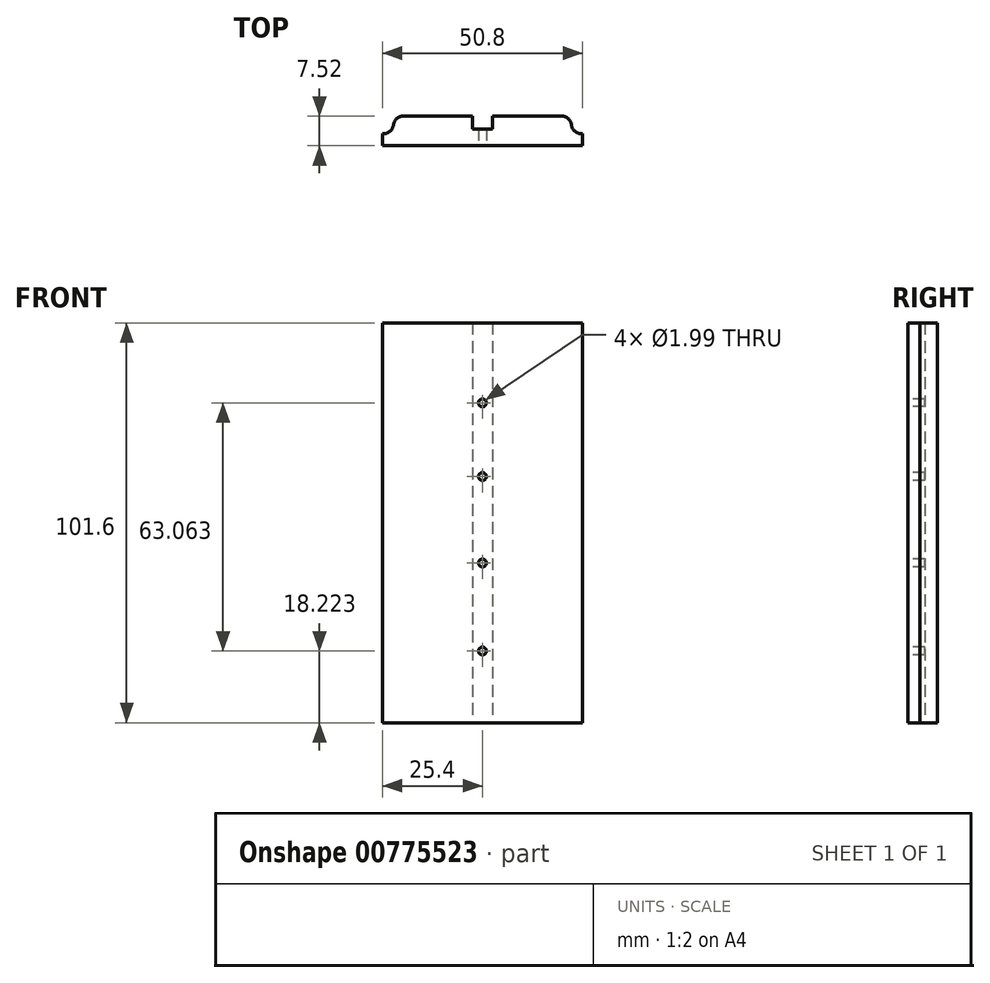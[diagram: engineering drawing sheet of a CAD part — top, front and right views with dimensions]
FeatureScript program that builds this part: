
annotation { "Feature Type Name" : "Feature", "Feature Type Description" : "" }
export const myFeature = defineFeature(function(context is Context, id is Id, definition is map)
    precondition{}
    {
        {
            var Q0;
            Q0=qCreatedBy(makeId("Top.planeOp"),FACE);
            var sketch = newSketch(context, id + "F0", { "sketchPlane" : qUnion([Q0])});
            skLineSegment(sketch, "E0", {"start": v(0, -10.22) * mm, "end": v(0, 14.45) * mm, "construction": true});
            skLineSegment(sketch, "E1", {"start": v(0, 0) * mm, "end": v(-25.4, 0) * mm});
            skLineSegment(sketch, "E2", {"start": v(-25.4, 0) * mm, "end": v(-25.4, 3.05) * mm});
            skLineSegment(sketch, "E3", {"start": v(-25.4, 3.05) * mm, "end": v(-22.63, 3.05) * mm});
            skLineSegment(sketch, "E4", {"start": v(-22.63, 3.05) * mm, "end": v(-22.63, 7.52) * mm});
            skLineSegment(sketch, "E5", {"start": v(-22.63, 7.52) * mm, "end": v(-2.54, 7.52) * mm});
            skLineSegment(sketch, "E6", {"start": v(-2.54, 7.52) * mm, "end": v(-2.54, 4.3) * mm});
            skLineSegment(sketch, "E7", {"start": v(-2.54, 4.3) * mm, "end": v(0, 4.3) * mm});
            skLineSegment(sketch, "E8.MirrorCS", {"start": v(25.4, 3.05) * mm, "end": v(22.63, 3.05) * mm});
            skLineSegment(sketch, "E9.MirrorCS", {"start": v(25.4, 0) * mm, "end": v(25.4, 3.05) * mm});
            skLineSegment(sketch, "E10.MirrorCS", {"start": v(2.54, 7.52) * mm, "end": v(2.54, 4.3) * mm});
            skLineSegment(sketch, "E11.MirrorCS", {"start": v(2.54, 4.3) * mm, "end": v(0, 4.3) * mm});
            skLineSegment(sketch, "E12.MirrorCS", {"start": v(0, 0) * mm, "end": v(25.4, 0) * mm});
            skLineSegment(sketch, "E13.MirrorCS", {"start": v(22.63, 7.52) * mm, "end": v(2.54, 7.52) * mm});
            skLineSegment(sketch, "E14.MirrorCS", {"start": v(22.63, 3.05) * mm, "end": v(22.63, 7.52) * mm});
            skSolve(sketch);
        }
        {
            var Q0;
            Q0=makeQuery(id+"F0.imprint","IMPRINT",FACE,{"disambiguationData":[TD([[makeQuery(id+"F0.imprint","IMPRINT",EDGE,{"derivedFrom":sQuery(id+"F0.wireOp",EDGE,"E1")}),-1.0]])]});
            extrude(context, id + "F1", {"entities" : qUnion([Q0]), "depth" : 101.6 * mm, "offsetDistance" : 25.4 * mm});
        }
        {
            var Q0;
            Q0=makeQuery(id+"F1.opExtrude","SWEPT_EDGE",EDGE,{"disambiguationData":[OSD([sQuery(id+"F0.wireOp",EDGE,"E13.MirrorCS"),sQuery(id+"F0.wireOp",EDGE,"E14.MirrorCS")])]});
            fillet(context, id + "F2", {"entities" : qUnion([Q0]), "radius" : 2.54 * mm, "tangentPropagation" : true, "allowEdgeOverflow" : false});
        }
        {
            var Q0;
            Q0=makeQuery(id+"F1.opExtrude","SWEPT_EDGE",EDGE,{"disambiguationData":[OSD([sQuery(id+"F0.wireOp",EDGE,"E8.MirrorCS"),sQuery(id+"F0.wireOp",EDGE,"E14.MirrorCS")])]});
            fillet(context, id + "F3", {"entities" : qUnion([Q0]), "radius" : 2.54 * mm, "tangentPropagation" : true, "allowEdgeOverflow" : false});
        }
        {
            var Q0;
            Q0=makeQuery(id+"F1.opExtrude","SWEPT_EDGE",EDGE,{"disambiguationData":[OSD([sQuery(id+"F0.wireOp",EDGE,"E4"),sQuery(id+"F0.wireOp",EDGE,"E5")])]});
            fillet(context, id + "F4", {"entities" : qUnion([Q0]), "radius" : 2.54 * mm, "tangentPropagation" : true, "allowEdgeOverflow" : false});
        }
        {
            var Q0;
            Q0=makeQuery(id+"F1.opExtrude","SWEPT_EDGE",EDGE,{"disambiguationData":[OSD([sQuery(id+"F0.wireOp",EDGE,"E3"),sQuery(id+"F0.wireOp",EDGE,"E4")])]});
            var Q1;
            {var subQ0=sQuery(id+"F0.wireOp",EDGE,"E4");Q1=makeQuery(id+"F4.opFillet","BLEND_EDGE",EDGE,{"blendedFrom":[makeQuery(id+"F1.opExtrude","SWEPT_EDGE",EDGE,{"disambiguationData":[OSD([subQ0,sQuery(id+"F0.wireOp",EDGE,"E5")])]}),makeQuery(id+"F1.opExtrude","SWEPT_FACE",FACE,{"disambiguationData":[OSD([subQ0])]})],"blendedInto":[makeQuery(id+"F1.opExtrude","SWEPT_FACE",FACE,{"disambiguationData":[OSD([subQ0])]})]});}
            fillet(context, id + "F5", {"entities" : qUnion([Q0, Q1]), "radius" : 2.54 * mm, "tangentPropagation" : true, "allowEdgeOverflow" : false});
        }
        {
            var Q0;
            Q0=makeQuery(id+"F1.opExtrude","SWEPT_FACE",FACE,{"disambiguationData":[OSD([sQuery(id+"F0.wireOp",EDGE,"E1"),sQuery(id+"F0.wireOp",EDGE,"E12.MirrorCS")])]});
            var sketch = newSketch(context, id + "F6", { "sketchPlane" : qUnion([Q0])});
            skLineSegment(sketch, "E15", {"start": v(0, 0) * mm, "end": v(0, 101.6) * mm, "construction": true});
            skPoint(sketch, "E16", {"position": v(0, 81.29) * mm});
            skPoint(sketch, "E17", {"position": v(0, 18.22) * mm});
            skPoint(sketch, "E18", {"position": v(0, 40.6) * mm});
            skPoint(sketch, "E19", {"position": v(0, 62.55) * mm});
            skSolve(sketch);
        }
        {
            var Q0;
            Q0=sQuery(id+"F6.wireOp",VERTEX,"E16");
            var Q1;
            Q1=sQuery(id+"F6.wireOp",VERTEX,"E19");
            var Q2;
            Q2=sQuery(id+"F6.wireOp",VERTEX,"E18");
            var Q3;
            Q3=sQuery(id+"F6.wireOp",VERTEX,"E17");
            var Q4;
            Q4=makeQuery(id+"F1.opExtrude","SWEPT_BODY",BODY,{"disambiguationData":[OSD([sQuery(id+"F0.wireOp",EDGE,"E1"),sQuery(id+"F0.wireOp",EDGE,"E2"),sQuery(id+"F0.wireOp",EDGE,"E3"),sQuery(id+"F0.wireOp",EDGE,"E4"),sQuery(id+"F0.wireOp",EDGE,"E5"),sQuery(id+"F0.wireOp",EDGE,"E6"),sQuery(id+"F0.wireOp",EDGE,"E7"),sQuery(id+"F0.wireOp",EDGE,"E8.MirrorCS"),sQuery(id+"F0.wireOp",EDGE,"E9.MirrorCS"),sQuery(id+"F0.wireOp",EDGE,"E10.MirrorCS"),sQuery(id+"F0.wireOp",EDGE,"E11.MirrorCS"),sQuery(id+"F0.wireOp",EDGE,"E12.MirrorCS"),sQuery(id+"F0.wireOp",EDGE,"E13.MirrorCS"),sQuery(id+"F0.wireOp",EDGE,"E14.MirrorCS")])]});
            hole(context, id + "F7", {"style" : HoleStyle.SIMPLE, "endStyle" : HoleEndStyle.THROUGH, "standardTappedOrClearance" : lookupTablePath({ "standard" : "ANSI", "engagement" : "75%", "pitch" : "48 tpi", "size" : "#3", "type" : "Tapped" }), "standardBlindInLast" : lookupTablePath({ "standard" : "ANSI", "engagement" : "75%", "pitch" : "48 tpi", "size" : "#3", "type" : "Tapped" }), "holeDiameter" : 2 * mm, "majorDiameter" : 2.5 * mm, "showTappedDepth" : true, "isTappedThrough" : true, "tappedDepth" : 12.7 * mm, "tapClearance" : 3, "locations" : qUnion([Q0, Q1, Q2, Q3]), "scope" : qUnion([Q4])});
        }
    });
